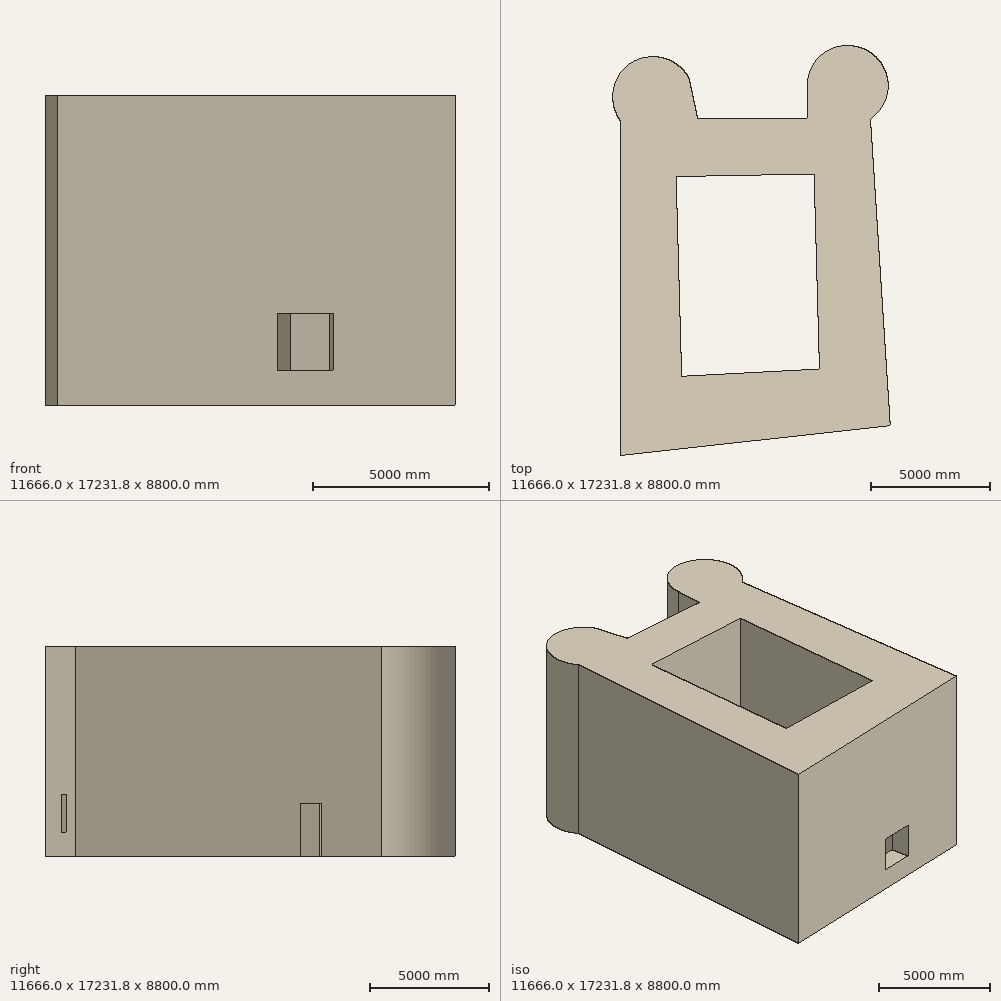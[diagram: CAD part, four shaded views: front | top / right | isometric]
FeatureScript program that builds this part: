
annotation { "Feature Type Name" : "Feature", "Feature Type Description" : "" }
export const myFeature = defineFeature(function(context is Context, id is Id, definition is map)
    precondition{}
    {
        {
            var Q0;
            Q0=qCreatedBy(makeId("Top.planeOp"),FACE);
            var sketch = newSketch(context, id + "F0", { "sketchPlane" : qUnion([Q0])});
            skLineSegment(sketch, "E0", {"start": v(0, 0) * mm, "end": v(0, 14200) * mm, "construction": true});
            skLineSegment(sketch, "E1", {"start": v(0, 14200) * mm, "end": v(10499.73, 14125) * mm, "construction": true});
            skLineSegment(sketch, "E2", {"start": v(10499.73, 14125) * mm, "end": v(11331.06, 1251.82) * mm});
            skLineSegment(sketch, "E3", {"start": v(11331.06, 1251.82) * mm, "end": v(0, 0) * mm});
            skLineSegment(sketch, "E4", {"start": v(2330.4, 11724.26) * mm, "end": v(8129.45, 11828.97) * mm});
            skLineSegment(sketch, "E5", {"start": v(8129.45, 11828.97) * mm, "end": v(8354.79, 3632.07) * mm});
            skLineSegment(sketch, "E6", {"start": v(8354.79, 3632.07) * mm, "end": v(2562.79, 3327.48) * mm});
            skLineSegment(sketch, "E7", {"start": v(2562.79, 3327.48) * mm, "end": v(2330.4, 11724.26) * mm});
            skArc(sketch, "E8", {"start": v(2877.8, 15838.84) * mm, "mid": v(467.57, 16507.05) * mm, "end": v(0, 14050) * mm});
            skArc(sketch, "E9", {"start": v(10499.73, 14125) * mm, "mid": v(10346.87, 17031.06) * mm, "end": v(7845.44, 15544) * mm});
            skLineSegment(sketch, "E10", {"start": v(7845.44, 15544) * mm, "end": v(7835.44, 14144.03) * mm});
            skLineSegment(sketch, "E11", {"start": v(2877.8, 15838.84) * mm, "end": v(3731.7, 14173.34) * mm, "construction": true});
            skLineSegment(sketch, "E12", {"start": v(2877.8, 15838.84) * mm, "end": v(3235.44, 14176.89) * mm});
            skLineSegment(sketch, "E13", {"start": v(3235.44, 14176.89) * mm, "end": v(7835.44, 14144.03) * mm});
            skLineSegment(sketch, "E14", {"start": v(0, 14050) * mm, "end": v(0, 0) * mm});
            skSolve(sketch);
        }
        {
            var Q0;
            Q0 = qSketchRegion(id + "F0", true);
            extrude(context, id + "F1", {"entities" : qUnion([Q0]), "depth" : 8800 * mm});
        }
        {
            var Q0;
            Q0=makeQuery(id+"F1.opExtrude","CAP_FACE",FACE,{"disambiguationData":[OSD([sQuery(id+"F0.wireOp",EDGE,"E2"),sQuery(id+"F0.wireOp",EDGE,"E3"),sQuery(id+"F0.wireOp",EDGE,"E4"),sQuery(id+"F0.wireOp",EDGE,"E5"),sQuery(id+"F0.wireOp",EDGE,"E6"),sQuery(id+"F0.wireOp",EDGE,"E7"),sQuery(id+"F0.wireOp",EDGE,"E8"),sQuery(id+"F0.wireOp",EDGE,"E9"),sQuery(id+"F0.wireOp",EDGE,"E10"),sQuery(id+"F0.wireOp",EDGE,"E12"),sQuery(id+"F0.wireOp",EDGE,"E13"),sQuery(id+"F0.wireOp",EDGE,"E14")])],"isStart":true});
            cPlane(context, id + "F2", {"entities" : qUnion([Q0]), "cplaneType" : CPlaneType.OFFSET, "offset" : 1000 * mm, "oppositeDirection" : true, "width" : 150 * mm, "height" : 150 * mm});
        }
        {
            var Q0;
            Q0=qCreatedBy(id+"F2.planeOp",FACE);
            var sketch = newSketch(context, id + "F3", { "sketchPlane" : qUnion([Q0])});
            skLineSegment(sketch, "E15", {"start": v(4935.44, -14164.75) * mm, "end": v(4931.15, -13564.76) * mm});
            skLineSegment(sketch, "E16", {"start": v(6131.15, -13556.19) * mm, "end": v(6135.44, -14156.17) * mm});
            skLineSegment(sketch, "E17", {"start": v(6135.44, -14156.17) * mm, "end": v(4935.44, -14164.75) * mm});
            skLineSegment(sketch, "E18", {"start": v(6261.9, -691.8) * mm, "end": v(7852.23, -867.49) * mm});
            skLineSegment(sketch, "E19", {"start": v(7852.23, -867.49) * mm, "end": v(7753.4, -1762.04) * mm});
            skLineSegment(sketch, "E20", {"start": v(6163.08, -1586.35) * mm, "end": v(6261.9, -691.8) * mm});
            skLineSegment(sketch, "E21", {"start": v(6163.08, -1586.35) * mm, "end": v(7753.4, -1762.04) * mm});
            skLineSegment(sketch, "E22", {"start": v(4931.15, -13564.76) * mm, "end": v(6131.15, -13556.19) * mm});
            skSolve(sketch);
        }
        {
            var Q0;
            Q0 = qSketchRegion(id + "F3", true);
            extrude(context, id + "F4", {"entities" : qUnion([Q0]), "operationType" : NewBodyOperationType.REMOVE, "oppositeDirection" : true, "depth" : 1600 * mm});
        }
        {
            var Q0;
            Q0=qCreatedBy(makeId("Top.planeOp"),FACE);
            var sketch = newSketch(context, id + "F5", { "sketchPlane" : qUnion([Q0])});
            skLineSegment(sketch, "E23", {"start": v(5362.79, 3474.73) * mm, "end": v(6163.08, 1586.35) * mm});
            skLineSegment(sketch, "E24", {"start": v(6163.08, 1586.35) * mm, "end": v(7753.4, 1762.04) * mm});
            skLineSegment(sketch, "E25", {"start": v(7753.4, 1762.04) * mm, "end": v(7854.79, 3605.77) * mm});
            skLineSegment(sketch, "E26", {"start": v(7854.79, 3605.77) * mm, "end": v(5362.79, 3474.73) * mm});
            skLineSegment(sketch, "E27", {"start": v(4931.15, 13564.76) * mm, "end": v(4230.4, 11758.57) * mm});
            skLineSegment(sketch, "E28", {"start": v(4230.4, 11758.57) * mm, "end": v(6629.45, 11801.89) * mm});
            skLineSegment(sketch, "E29", {"start": v(6629.45, 11801.89) * mm, "end": v(6131.15, 13556.19) * mm});
            skLineSegment(sketch, "E30", {"start": v(6131.15, 13556.19) * mm, "end": v(4931.15, 13564.76) * mm});
            skSolve(sketch);
        }
        {
            var Q0;
            Q0 = qSketchRegion(id + "F5", true);
            extrude(context, id + "F6", {"entities" : qUnion([Q0]), "operationType" : NewBodyOperationType.REMOVE, "depth" : 2600 * mm});
        }
        {
            var Q0;
            Q0=makeQuery(id+"F1.opExtrude","SWEPT_FACE",FACE,{"disambiguationData":[OSD([sQuery(id+"F0.wireOp",EDGE,"E5")])]});
            var sketch = newSketch(context, id + "F7", { "sketchPlane" : qUnion([Q0])});
            skLineSegment(sketch, "E31.bottom", {"start": v(-11301.1, 0) * mm, "end": v(-10401.1, 0) * mm});
            skLineSegment(sketch, "E31.top", {"start": v(-11301.1, 2200) * mm, "end": v(-10401.1, 2200) * mm});
            skLineSegment(sketch, "E31.left", {"start": v(-11301.1, 0) * mm, "end": v(-11301.1, 2200) * mm});
            skLineSegment(sketch, "E31.right", {"start": v(-10401.1, 0) * mm, "end": v(-10401.1, 2200) * mm});
            skSolve(sketch);
        }
        {
            var Q0;
            Q0 = qSketchRegion(id + "F7", true);
            extrude(context, id + "F8", {"entities" : qUnion([Q0]), "operationType" : NewBodyOperationType.REMOVE, "endBound" : BoundingType.UP_TO_NEXT, "oppositeDirection" : true, "depth" : 25 * mm});
        }
    });
